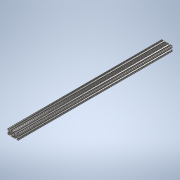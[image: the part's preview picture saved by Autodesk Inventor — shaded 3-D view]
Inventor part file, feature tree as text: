
AUTODESK INVENTOR PART (.ipt)
format: ipt  version: 2020 (Build 240168000, 168)  size: 357,376 bytes
history: native  units: in
note: dims shown in document units (in); Inventor stores cm internally (conversion verified against a paired STEP export)
features: sketch x2, extrude x1
ambient origin geometry x8: Origin, YZ Plane, XZ Plane, XY Plane, X Axis, Y Axis, Z Axis, Center Point
bodies: Solid1 (feature_tree)
feature tree (3):
  extrude  "Extrusion1"  [1 undecoded]
  sketch  "Sketch2"
  sketch  "Sketch1"  dims[d0=28.0in d1=0.0in]
note: 1 required parameter value undecoded (feature->parameter linkage not recoverable at this tier; creation-order binding heuristic only, values carry confidence <= 0.55)
